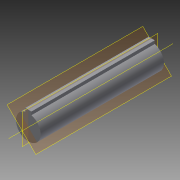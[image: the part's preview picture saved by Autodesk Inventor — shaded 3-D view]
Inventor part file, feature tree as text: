
AUTODESK INVENTOR PART (.ipt)
format: ipt  version: 2015 (Build 190159000, 159)  size: 83,968 bytes
history: native  units: in
note: dims shown in document units (in); Inventor stores cm internally (conversion verified against a paired STEP export)
features: plane x3, extrude x1, sketch x1
ambient origin geometry x8: Origin, YZ Plane, XZ Plane, XY Plane, X Axis, Y Axis, Z Axis, Center Point
bodies: Solid1 (feature_tree)
feature tree (5):
  extrude  "Extrusion1"  Depth=0.25in
  plane  "Work Plane1"
  plane  "Work Plane2"
  plane  "Work Plane3"
  sketch  "Sketch1"  dims[d0=1.0in d1=0.25in d2=0.13in d3=5.0in d4=0.0in d5=-0.3092in d6=45.0deg]
